# Revit family: Mirror-Vitra-ValarteSeries-62213+62214+62215+62216+62217+62218+62219+62220+62221+62222+62223+62224
name_source: partatom
category: Furniture Systems
revit_build: Autodesk Revit 2017 (Build: 20160225_1515(x64)
units: mm (PartAtom-declared; Revit-internal decimal feet)

## family parameters
Cut with Voids When Loaded = No
Host = Face
OmniClass Number = 23.40.00.00
OmniClass Title = Equipment and Furnishings
Part Type = Normal
Room Calculation Point = No
Round Connector Dimension = Use Diameter
Shared = Yes

## types (12) — shared parameters
BIMobject category = Mirrors
Construction Type = Face Mounted
Default Elevation = 1200 mm
Depth(mm) = 30 mm  [stored 0.0984252 ft]
Description = Valarte Mirror
Design country = Turkey
Height(mm) = 700 mm  [stored 2.29659 ft]
IFC Classification = Furniture
Manufacturer = Vitra
Manufacturer name = Vitra
Masterformat 2014 Code = 08 83 00
Masterformat 2014 Description = Mirrors
Nominal height = 0.000
Nominal width = 0.000
OmniClass Code = 23-21 00 00
OmniClass Description = Furnishings, Fixtures and Equipment Products
Product certification = https://vitraglobal.com
Product data url = https://www.vitra.com.tr
Product family = Valarte
Product group = Mirror
Secondary Material = Vitra-Mirror
Technical description = https://www.vitra.com.tr
UNSPSC Code = 56
UNSPSC Description = Mirrors
URL = https://vitraglobal.com
Uniclass 1.4 Code = L8732
Uniclass 1.4 Description = Mirrors
Uniclass 2.0 Code = PR-71-55
Uniclass 2.0 Description = Mirrors
Uniclass 2015 Code = Pr_25_71_53
Uniclass 2015 Name = Mirrors
Uniformat II Code = E20
Uniformat II Description = FURNISHINGS
Warranty Period (Year) = 2
Weight Net (kg) = 10,000
Youtube = https://www.youtube.com

## per-type parameters (varying)
| type | Article No. (default) | Model | Primary Material | Product SKU | Width(mm) |
| Mirror-65cm-MatteWhite-Vitra-ValarteSeries_62213 | 62213 | 62213 | Vitra-MattWhite | 62213 | 595 mm  [stored 1.9521 ft] |
| Mirror-65cm-MatteGrey-Vitra-ValarteSeries_62214 | 62214 | 62214 | Vitra-MattGrey | 62214 | 595 mm  [stored 1.9521 ft] |
| Mirror-65cm-MatteIvory-Vitra-ValarteSeries_62215 | 62215 | 62215 | Vitra-MattIvory | 62215 | 595 mm  [stored 1.9521 ft] |
| Mirror-80cm-MatteWhite-Vitra-ValarteSeries_62216 | 62216 | 62216 | Vitra-MattWhite | 62216 | 745 mm  [stored 2.44423 ft] |
| Mirror-80cm-MatteGrey-Vitra-ValarteSeries_62217 | 62217 | 62217 | Vitra-MattGrey | 62217 | 745 mm  [stored 2.44423 ft] |
| Mirror-80cm-MatteIvory-Vitra-ValarteSeries_62218 | 62218 | 62218 | Vitra-MattIvory | 62218 | 745 mm  [stored 2.44423 ft] |
| Mirror-100cm-MatteWhite-Vitra-ValarteSeries_62219 | 62219 | 62219 | Vitra-MattWhite | 62219 | 945 mm  [stored 3.10039 ft] |
| Mirror-100cm-MatteGrey-Vitra-ValarteSeries_62220 | 62220 | 62220 | Vitra-MattGrey | 62220 | 945 mm  [stored 3.10039 ft] |
| Mirror-100cm-MatteIvory-Vitra-ValarteSeries_62221 | 62221 | 62221 | Vitra-MattIvory | 62221 | 945 mm  [stored 3.10039 ft] |
| Mirror-120cm-MatteWhite-Vitra-ValarteSeries_62222 | 62222 | 62222 | Vitra-MattWhite | 62222 | 1145 mm  [stored 3.75656 ft] |
| Mirror-120cm-MatteGrey-Vitra-ValarteSeries_62223 | 62223 | 62223 | Vitra-MattGrey | 62223 | 1145 mm  [stored 3.75656 ft] |
| Mirror-120cm-MatteIvory-Vitra-ValarteSeries_62224 | 62224 | 62224 | Vitra-MattIvory | 62224 | 1145 mm  [stored 3.75656 ft] |

note: [stored X ft] marks values corroborated as IEEE doubles in the binary element streams (Revit-internal decimal feet)

## geometry (parser evidence)
native form markers: Sweep x3
no freeform markers — native parametric forms only
